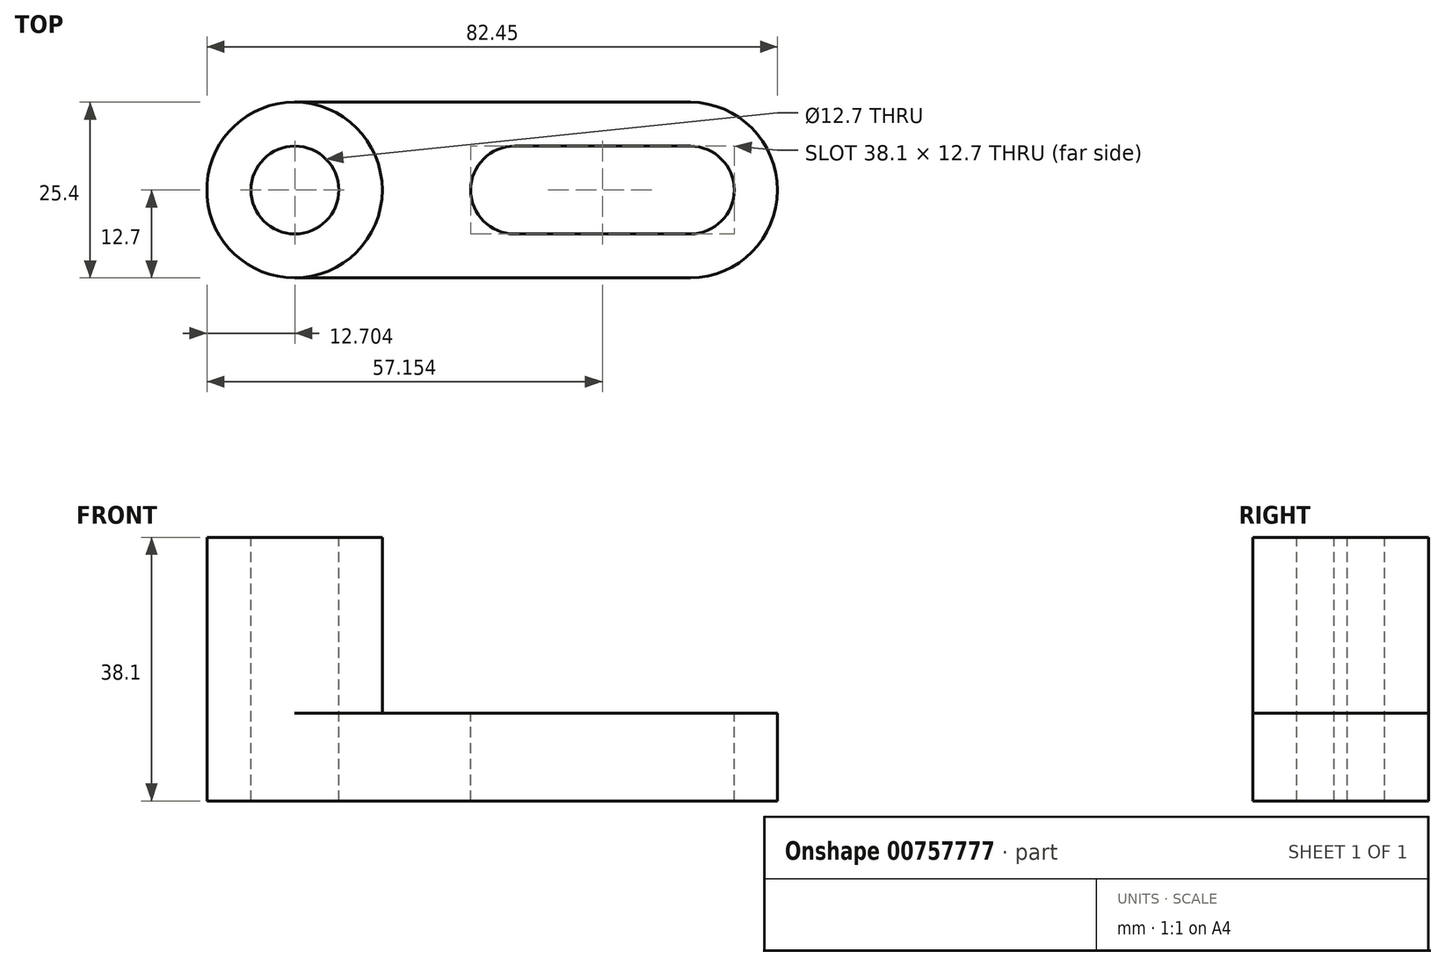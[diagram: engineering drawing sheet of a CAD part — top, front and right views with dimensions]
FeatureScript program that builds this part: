
annotation { "Feature Type Name" : "Feature", "Feature Type Description" : "" }
export const myFeature = defineFeature(function(context is Context, id is Id, definition is map)
    precondition{}
    {
        {
            var Q0;
            Q0=qCreatedBy(makeId("Front.planeOp"),FACE);
            var sketch = newSketch(context, id + "F0", { "sketchPlane" : qUnion([Q0])});
            skLineSegment(sketch, "E0", {"start": v(36.36, 0) * mm, "end": v(-46.19, 0) * mm});
            skLineSegment(sketch, "E1", {"start": v(-46.19, 0) * mm, "end": v(-46.19, 38.1) * mm});
            skLineSegment(sketch, "E2", {"start": v(-46.19, 38.1) * mm, "end": v(-20.79, 38.1) * mm});
            skLineSegment(sketch, "E3", {"start": v(-20.79, 38.1) * mm, "end": v(-20.79, 12.7) * mm});
            skLineSegment(sketch, "E4", {"start": v(-20.79, 12.7) * mm, "end": v(36.36, 12.7) * mm});
            skLineSegment(sketch, "E5", {"start": v(36.36, 12.7) * mm, "end": v(36.36, 0) * mm});
            skSolve(sketch);
        }
        {
            var Q0;
            Q0 = qSketchRegion(id + "F0", true);
            extrude(context, id + "F1", {"entities" : qUnion([Q0]), "depth" : 25.4 * mm, "offsetDistance" : 25.4 * mm});
        }
        {
            var Q0;
            Q0=makeQuery(id+"F1.opExtrude","SWEPT_FACE",FACE,{"disambiguationData":[OSD([sQuery(id+"F0.wireOp",EDGE,"E2")])]});
            var sketch = newSketch(context, id + "F2", { "sketchPlane" : qUnion([Q0])});
            skLineSegment(sketch, "E6", {"start": v(-33.49, -25.4) * mm, "end": v(-33.49, 0) * mm});
            skCircle(sketch, "E7", {"center": v(-33.49, -12.7) * mm, "radius": 6.35 * mm});
            skArc(sketch, "E8", {"start": v(-33.49, 0) * mm, "mid": v(-46.22, -12.7) * mm, "end": v(-33.49, -25.4) * mm});
            skSolve(sketch);
        }
        {
            var Q0;
            {var subQ0=sQuery(id+"F2.wireOp",EDGE,"E7");var subQ1=sQuery(id+"F2.wireOp",EDGE,"E6");var subQ2=makeQuery(id+"F2.imprint","INTERSECT",VERTEX,{"disambiguationData":[OD(0.0)],"derivedFrom":[subQ1,subQ0]});Q0=makeQuery(id+"F2.imprint","IMPRINT",FACE,{"disambiguationData":[TD([[makeQuery(id+"F2.imprint","IMPRINT",EDGE,{"disambiguationData":[TD([[subQ2,-1.0]])],"derivedFrom":subQ1}),1.0]])]});}
            var Q1;
            {var subQ0=sQuery(id+"F2.wireOp",EDGE,"E7");var subQ1=sQuery(id+"F2.wireOp",EDGE,"E6");var subQ2=makeQuery(id+"F2.imprint","INTERSECT",VERTEX,{"disambiguationData":[OD(0.0)],"derivedFrom":[subQ1,subQ0]});Q1=makeQuery(id+"F2.imprint","IMPRINT",FACE,{"disambiguationData":[TD([[makeQuery(id+"F2.imprint","IMPRINT",EDGE,{"disambiguationData":[TD([[subQ2,-1.0]])],"derivedFrom":subQ1}),-1.0]])]});}
            var Q2;
            {var subQ0=sQuery(id+"F2.wireOp",EDGE,"E8");var subQ1=makeQuery(id+"F1.opExtrude","SWEPT_EDGE",EDGE,{"disambiguationData":[OSD([sQuery(id+"F0.wireOp",EDGE,"E1"),sQuery(id+"F0.wireOp",EDGE,"E2")])]});var subQ2=makeQuery(id+"F2.imprint","INTERSECT",VERTEX,{"disambiguationData":[OD(0.0)],"derivedFrom":[subQ1,subQ0]});Q2=makeQuery(id+"F2.imprint","IMPRINT",FACE,{"disambiguationData":[TD([[makeQuery(id+"F2.imprint","IMPRINT",EDGE,{"disambiguationData":[TD([[subQ2,-1.0]])],"derivedFrom":subQ0}),1.0]])]});}
            var Q3;
            {var subQ0=sQuery(id+"F2.wireOp",EDGE,"E8");var subQ1=sQuery(id+"F0.wireOp",EDGE,"E2");var subQ2=makeQuery(id+"F1.opExtrude","CAP_EDGE",EDGE,{"disambiguationData":[OSD([subQ1])],"isStart":false});var subQ3=makeQuery(id+"F2.imprint","INTERSECT",VERTEX,{"derivedFrom":[subQ2,subQ0]});Q3=makeQuery(id+"F2.imprint","IMPRINT",FACE,{"disambiguationData":[TD([[makeQuery(id+"F2.imprint","IMPRINT",EDGE,{"disambiguationData":[TD([[subQ3,1.0]])],"derivedFrom":subQ0}),-1.0]])]});}
            var Q4;
            {var subQ0=sQuery(id+"F2.wireOp",EDGE,"E8");var subQ1=sQuery(id+"F0.wireOp",EDGE,"E2");var subQ4=makeQuery(id+"F1.opExtrude","SWEPT_EDGE",EDGE,{"disambiguationData":[OSD([sQuery(id+"F0.wireOp",EDGE,"E1"),subQ1])]});var subQ5=makeQuery(id+"F2.imprint","INTERSECT",VERTEX,{"disambiguationData":[OD(0.0)],"derivedFrom":[subQ4,subQ0]});Q4=makeQuery(id+"F2.imprint","IMPRINT",FACE,{"disambiguationData":[TD([[makeQuery(id+"F2.imprint","IMPRINT",EDGE,{"disambiguationData":[TD([[subQ5,1.0]])],"derivedFrom":subQ0}),-1.0]])]});}
            extrude(context, id + "F3", {"entities" : qUnion([Q0, Q1, Q2, Q3, Q4]), "operationType" : NewBodyOperationType.REMOVE, "endBound" : BoundingType.THROUGH_ALL, "oppositeDirection" : true, "depth" : 25.4 * mm, "offsetDistance" : 25.4 * mm});
        }
        {
            var Q0;
            Q0=makeQuery(id+"F1.opExtrude","SWEPT_FACE",FACE,{"disambiguationData":[OSD([sQuery(id+"F0.wireOp",EDGE,"E2")])]});
            var sketch = newSketch(context, id + "F4", { "sketchPlane" : qUnion([Q0])});
            skArc(sketch, "E9", {"start": v(-33.56, -25.4) * mm, "mid": v(-20.86, -12.7) * mm, "end": v(-33.56, 0) * mm});
            skSolve(sketch);
        }
        {
            var Q0;
            Q0 = qSketchRegion(id + "F4", true);
            var Q1;
            Q1=makeQuery(id+"F4.imprint","IMPRINT",FACE,{"disambiguationData":[TD([[makeQuery(id+"F4.imprint","IMPRINT",EDGE,{"derivedFrom":sQuery(id+"F4.wireOp",EDGE,"E9")}),-1.0]])]});
            extrude(context, id + "F5", {"entities" : qUnion([Q0, Q1]), "operationType" : NewBodyOperationType.REMOVE, "oppositeDirection" : true, "depth" : 25.4 * mm, "offsetDistance" : 25.4 * mm});
        }
        {
            var Q0;
            Q0=makeQuery(id+"F5.boolean.opBoolean","MERGE",FACE,{"derivedFrom":[makeQuery(id+"F1.opExtrude","SWEPT_FACE",FACE,{"disambiguationData":[OSD([sQuery(id+"F0.wireOp",EDGE,"E4")])]}),makeQuery(id+"F5.opExtrude","CAP_FACE",FACE,{"disambiguationData":[OSD([sQuery(id+"F0.wireOp",EDGE,"E2"),sQuery(id+"F0.wireOp",EDGE,"E3"),sQuery(id+"F4.wireOp",EDGE,"E9")])],"isStart":false})]});
            var sketch = newSketch(context, id + "F6", { "sketchPlane" : qUnion([Q0])});
            skLineSegment(sketch, "E10", {"start": v(23.66, 0) * mm, "end": v(23.66, -25.4) * mm});
            skLineSegment(sketch, "E11", {"start": v(-1.74, 0) * mm, "end": v(-1.74, -25.4) * mm});
            skCircle(sketch, "E12", {"center": v(23.66, -12.7) * mm, "radius": 6.35 * mm});
            skCircle(sketch, "E13", {"center": v(-1.74, -12.7) * mm, "radius": 6.35 * mm});
            skLineSegment(sketch, "E14", {"start": v(-1.74, -6.35) * mm, "end": v(23.66, -6.35) * mm});
            skLineSegment(sketch, "E15", {"start": v(-1.74, -19.05) * mm, "end": v(23.66, -19.05) * mm});
            skArc(sketch, "E16", {"start": v(23.66, -25.4) * mm, "mid": v(36.26, -12.7) * mm, "end": v(23.66, 0) * mm});
            skSolve(sketch);
        }
        {
            var Q0;
            {var subQ0=sQuery(id+"F6.wireOp",EDGE,"E16");Q0=makeQuery(id+"F6.imprint","IMPRINT",FACE,{"disambiguationData":[TD([[makeQuery(id+"F6.imprint","IMPRINT",EDGE,{"derivedFrom":subQ0}),-1.0]])]});}
            var Q1;
            {var subQ0=sQuery(id+"F6.wireOp",EDGE,"E14");Q1=makeQuery(id+"F6.imprint","IMPRINT",FACE,{"disambiguationData":[TD([[makeQuery(id+"F6.imprint","IMPRINT",EDGE,{"derivedFrom":subQ0}),-1.0]])]});}
            var Q2;
            {var subQ0=sQuery(id+"F6.wireOp",EDGE,"E12");var subQ1=sQuery(id+"F6.wireOp",EDGE,"E10");var subQ2=makeQuery(id+"F6.imprint","INTERSECT",VERTEX,{"derivedFrom":[subQ1,subQ0,sQuery(id+"F6.wireOp",EDGE,"E14")]});Q2=makeQuery(id+"F6.imprint","IMPRINT",FACE,{"disambiguationData":[TD([[makeQuery(id+"F6.imprint","IMPRINT",EDGE,{"disambiguationData":[TD([[subQ2,-1.0]])],"derivedFrom":subQ1}),1.0]])]});}
            var Q3;
            {var subQ0=sQuery(id+"F6.wireOp",EDGE,"E12");var subQ1=sQuery(id+"F6.wireOp",EDGE,"E10");var subQ2=makeQuery(id+"F6.imprint","INTERSECT",VERTEX,{"derivedFrom":[subQ1,subQ0,sQuery(id+"F6.wireOp",EDGE,"E14")]});Q3=makeQuery(id+"F6.imprint","IMPRINT",FACE,{"disambiguationData":[TD([[makeQuery(id+"F6.imprint","IMPRINT",EDGE,{"disambiguationData":[TD([[subQ2,-1.0]])],"derivedFrom":subQ1}),-1.0]])]});}
            var Q4;
            {var subQ0=sQuery(id+"F6.wireOp",EDGE,"E13");var subQ1=sQuery(id+"F6.wireOp",EDGE,"E11");var subQ2=makeQuery(id+"F6.imprint","INTERSECT",VERTEX,{"derivedFrom":[subQ1,subQ0,sQuery(id+"F6.wireOp",EDGE,"E14")]});Q4=makeQuery(id+"F6.imprint","IMPRINT",FACE,{"disambiguationData":[TD([[makeQuery(id+"F6.imprint","IMPRINT",EDGE,{"disambiguationData":[TD([[subQ2,-1.0]])],"derivedFrom":subQ1}),1.0]])]});}
            var Q5;
            {var subQ0=sQuery(id+"F6.wireOp",EDGE,"E13");var subQ1=sQuery(id+"F6.wireOp",EDGE,"E11");var subQ2=makeQuery(id+"F6.imprint","INTERSECT",VERTEX,{"derivedFrom":[subQ1,subQ0,sQuery(id+"F6.wireOp",EDGE,"E14")]});Q5=makeQuery(id+"F6.imprint","IMPRINT",FACE,{"disambiguationData":[TD([[makeQuery(id+"F6.imprint","IMPRINT",EDGE,{"disambiguationData":[TD([[subQ2,-1.0]])],"derivedFrom":subQ1}),-1.0]])]});}
            extrude(context, id + "F7", {"entities" : qUnion([Q0, Q1, Q2, Q3, Q4, Q5]), "operationType" : NewBodyOperationType.REMOVE, "oppositeDirection" : true, "depth" : 25.4 * mm, "offsetDistance" : 25.4 * mm});
        }
    });
